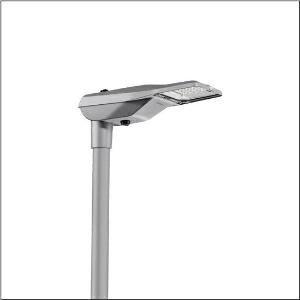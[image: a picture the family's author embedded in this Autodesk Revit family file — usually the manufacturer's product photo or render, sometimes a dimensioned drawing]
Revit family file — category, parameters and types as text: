
# Revit family: streetlight_sl_21_micro___st1_0ab_5xe1m33t08db_25ba
name_source: partatom
category: Lighting Fixtures
units: mm (PartAtom-declared; Revit-internal decimal feet)

## family parameters
Cut with Voids When Loaded = No
Host = Face
Light Source = No
Part Type = Normal
Room Calculation Point = No
Round Connector Dimension = Use Diameter
Shared = No

## types (1)
- --- (1 x LED, 4500 lm, 39.1 W, 3000K)
    Apparent Load = 39 VA
    CIE Flux Codes = 38 73 97 100 100
    Color Rendering = 70
    Color Temperature = 3000K
    Default Elevation = 1800 mm
    Description = Streetlight SL 21 micro, mast luminaire, primary light control with lens, of PMMA, primary optical cover: cover, of toughened safety glass, transparent, light distribution: ST1.0aB, light emission: direct distribution, primary light characteristic: asymmetric, installation type: side-entry, post-top, LED, High Power LED, rated luminous flux: 4.500lm, luminous efficacy: 115lm/W, light colour: 730, colour temperature: 3000K, control: flexible luminous flux parameterisation, time-dependent luminous flux control, constant luminous flux control, overheat protection, presetting dimming logarithmic, mains connection: 220..240V, AC, 50/60Hz, start of lifetime: 39W, end of service life: 41W, reduction: 18W, luminaire housing, of diecast aluminium, powder-coated, Siteco® metallic grey (DB 702S), corrosivity category C5 mid according to DIN EN ISO 12944, please order mast flange separately, inclination adjustable: 0°, 5°, 10°, 15°, sealing non-destructively replaceable, multi-level sealing system, length: 528mm, width: 235mm, height: 110mm, mast flange for spigot size: 42mm (side-entry): 5XC10008XM4, 60/48mm (side-entry/post-top): 5XC10108XM2, 76/60mm (side-entry/post-top): 5XC10108XM1, Smart Interface below and above, protection rating (complete): IP66, insulation class (complete): insulation class II (safety insulation), certification: CE, ENEC, ENEC+, VDE, impact resistance: IK09, permissible operating ambient temperature for outdoor applications: -40..+50°C, standard-compliant lighting for roads and squares, packaging unit: 1 piece

Light Distribution: ST1.0aB
    Height = 110 mm
    Lamp = 1 x LED
    Lamp Light Flux = 4500 lm
    Lamp Power = 39.1 W
    Lamp count = 1
    Length = 528 mm
    Luminous efficacy = 115 lm/W
    Manufacturer = Siteco
    ModVariant = No
    Model = 5XE1M33T08DB
    Number of Poles = 1
    OnlyDefault = Yes
    Power Factor = 1
    Product Name = Streetlight SL 21 micro | ST1.0aB
    Product group = mast luminaire | pylon top
    ProductGroupID = 6100
    Protection Class = Protection class II
    Protection Degree = IP 66
    RLX_Detail_Level = 1
    RLX_Emergency_Light_Flux = 0 lm
    RLX_Emergency_Type = 0
    RLX_Emergency_Type_DB = No
    RlxData = <blob elided: 98065 chars, md5=0b44fbfd>
    Socket = socket
    Standby Power = 0 W
    System Light Flux = 4500 lm
    System Power = 39 W
    Type Comments = factory setting: luminous flux: 100 % | dim-lin: 254 | 765 mA
    Type Image = l_1007239.jpg
    URL = http://relux.com
    VarID = @adj_104095
    Voltage = 0 V
    Weight = 0.00 kg
    Width = 235 mm

## geometry (parser evidence)
native form markers: Blend x4, Sweep x10
no freeform markers — native parametric forms only
